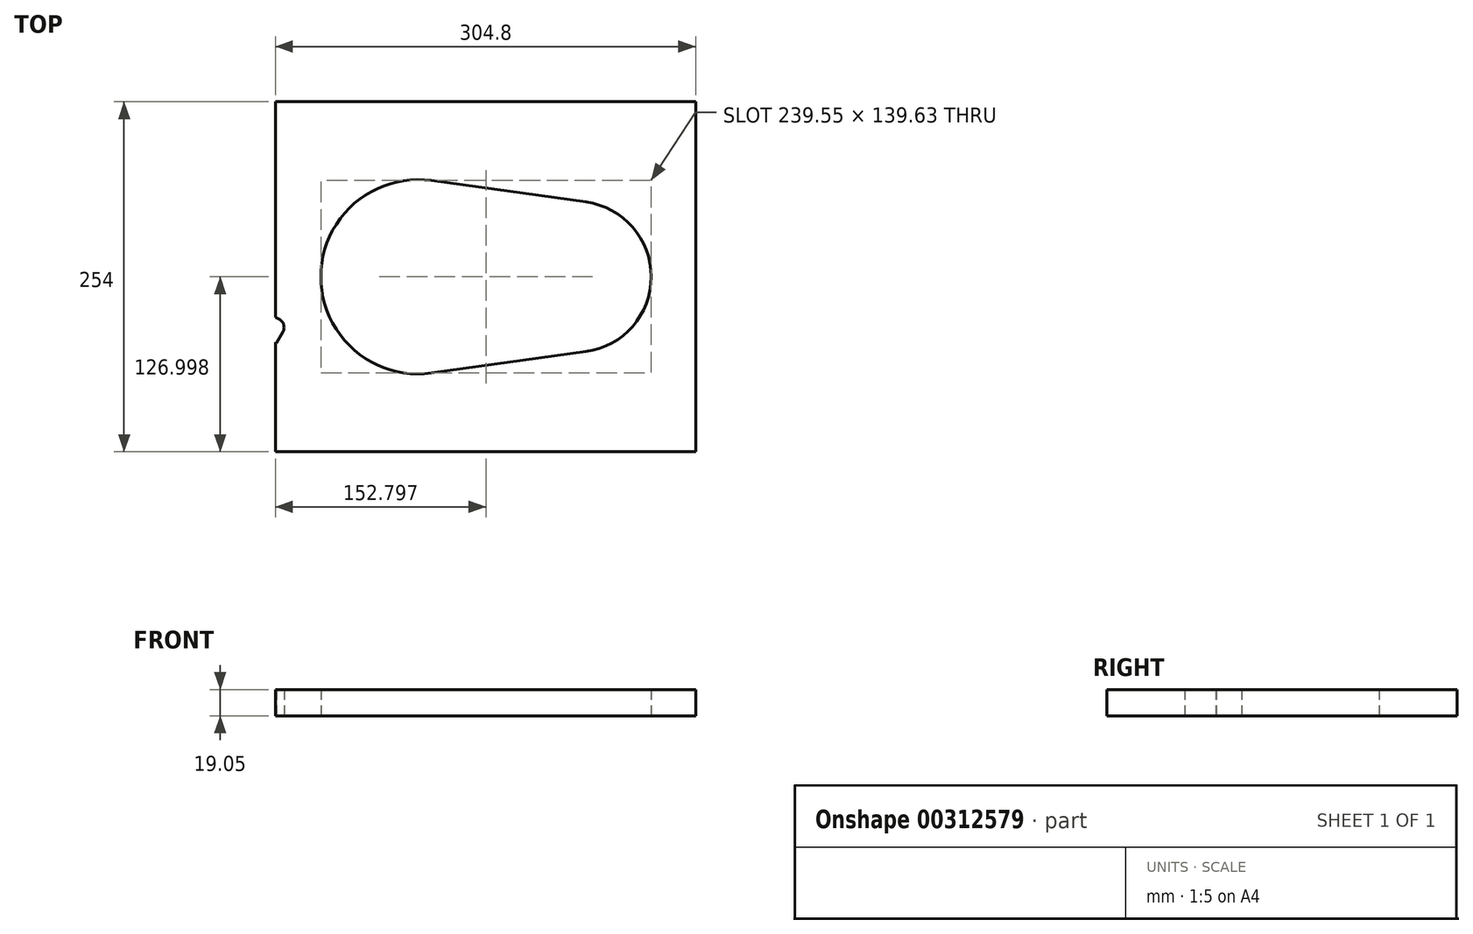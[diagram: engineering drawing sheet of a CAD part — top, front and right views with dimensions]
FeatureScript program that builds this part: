
annotation { "Feature Type Name" : "Feature", "Feature Type Description" : "" }
export const myFeature = defineFeature(function(context is Context, id is Id, definition is map)
    precondition{}
    {
        {
            var Q0;
            Q0=qCreatedBy(makeId("Top.planeOp"),FACE);
            var sketch = newSketch(context, id + "F0", { "sketchPlane" : qUnion([Q0])});
            skLineSegment(sketch, "E0", {"start": v(413.11, 329.58) * mm, "end": v(108.31, 329.58) * mm});
            skLineSegment(sketch, "E1", {"start": v(108.31, 329.58) * mm, "end": v(108.31, 75.58) * mm});
            skLineSegment(sketch, "E2", {"start": v(108.31, 75.58) * mm, "end": v(413.11, 75.58) * mm});
            skLineSegment(sketch, "E3", {"start": v(413.11, 329.58) * mm, "end": v(413.11, 75.58) * mm});
            skLineSegment(sketch, "E4", {"start": v(82.91, 329.58) * mm, "end": v(-221.89, 329.58) * mm});
            skLineSegment(sketch, "E5", {"start": v(-221.89, 329.58) * mm, "end": v(-221.89, 75.58) * mm});
            skLineSegment(sketch, "E6", {"start": v(-221.89, 75.58) * mm, "end": v(82.91, 75.58) * mm});
            skLineSegment(sketch, "E7", {"start": v(82.91, 329.58) * mm, "end": v(82.91, 75.58) * mm});
            skLineSegment(sketch, "E8", {"start": v(-173.23, 217.17) * mm, "end": v(-195.61, 223.17) * mm});
            skLineSegment(sketch, "E9", {"start": v(-173.23, 188) * mm, "end": v(-195.61, 182) * mm});
            skLineSegment(sketch, "E10", {"start": v(-195.61, 223.17) * mm, "end": v(-195.61, 182) * mm});
            skLineSegment(sketch, "E11", {"start": v(-133.37, 257.04) * mm, "end": v(-139.37, 279.42) * mm});
            skLineSegment(sketch, "E12", {"start": v(-104.19, 257.03) * mm, "end": v(-98.19, 279.42) * mm});
            skLineSegment(sketch, "E13", {"start": v(-98.19, 279.42) * mm, "end": v(-139.37, 279.42) * mm});
            skLineSegment(sketch, "E14", {"start": v(-133.37, 148.13) * mm, "end": v(-139.37, 125.75) * mm});
            skLineSegment(sketch, "E15", {"start": v(-104.19, 148.13) * mm, "end": v(-98.19, 125.75) * mm});
            skLineSegment(sketch, "E16", {"start": v(-98.19, 125.75) * mm, "end": v(-139.37, 125.75) * mm});
            skLineSegment(sketch, "E17", {"start": v(413.11, 68.19) * mm, "end": v(108.31, 68.19) * mm});
            skLineSegment(sketch, "E18", {"start": v(108.31, 68.19) * mm, "end": v(108.31, -185.81) * mm});
            skLineSegment(sketch, "E19", {"start": v(108.31, -185.81) * mm, "end": v(413.11, -185.81) * mm});
            skLineSegment(sketch, "E20", {"start": v(413.11, 68.19) * mm, "end": v(413.11, -185.81) * mm});
            skLineSegment(sketch, "E21", {"start": v(82.91, 68.19) * mm, "end": v(82.91, -185.81) * mm});
            skLineSegment(sketch, "E22", {"start": v(-221.89, -185.81) * mm, "end": v(82.91, -185.81) * mm});
            skLineSegment(sketch, "E23", {"start": v(-221.89, 68.19) * mm, "end": v(-221.89, -185.81) * mm});
            skLineSegment(sketch, "E24", {"start": v(82.91, 68.19) * mm, "end": v(-221.89, 68.19) * mm});
            skLineSegment(sketch, "E25", {"start": v(324.6, -113.27) * mm, "end": v(330.6, -135.65) * mm});
            skLineSegment(sketch, "E26", {"start": v(295.42, -113.26) * mm, "end": v(289.42, -135.65) * mm});
            skLineSegment(sketch, "E27", {"start": v(289.42, -135.65) * mm, "end": v(330.6, -135.65) * mm});
            skLineSegment(sketch, "E28", {"start": v(82.91, -136.8) * mm, "end": v(108.31, -136.8) * mm});
            skArc(sketch, "E29", {"start": v(187.78, 272.39) * mm, "mid": v(140.54, 218.14) * mm, "end": v(187.78, 163.9) * mm});
            skLineSegment(sketch, "E30", {"start": v(187.78, 163.9) * mm, "end": v(274.13, 151.9) * mm});
            skArc(sketch, "E31", {"start": v(274.13, 151.9) * mm, "mid": v(285.88, 145.55) * mm, "end": v(290.56, 133.04) * mm});
            skLineSegment(sketch, "E32", {"start": v(290.56, 133.04) * mm, "end": v(290.56, 122.9) * mm});
            skArc(sketch, "E33", {"start": v(290.56, 122.9) * mm, "mid": v(292.42, 118.4) * mm, "end": v(296.91, 116.54) * mm});
            skLineSegment(sketch, "E34", {"start": v(296.91, 116.54) * mm, "end": v(306.44, 116.54) * mm});
            skLineSegment(sketch, "E35", {"start": v(306.44, 116.54) * mm, "end": v(306.44, 173.17) * mm});
            skArc(sketch, "E36", {"start": v(306.44, 173.17) * mm, "mid": v(309.61, 263.23) * mm, "end": v(312.79, 173.17) * mm});
            skLineSegment(sketch, "E37", {"start": v(312.79, 173.17) * mm, "end": v(312.79, 116.54) * mm});
            skLineSegment(sketch, "E38", {"start": v(312.79, 116.54) * mm, "end": v(322.31, 116.54) * mm});
            skArc(sketch, "E39", {"start": v(322.31, 116.54) * mm, "mid": v(326.8, 118.4) * mm, "end": v(328.66, 122.9) * mm});
            skLineSegment(sketch, "E40", {"start": v(328.66, 122.9) * mm, "end": v(328.66, 137.12) * mm});
            skArc(sketch, "E41", {"start": v(328.66, 137.12) * mm, "mid": v(331.63, 147.33) * mm, "end": v(339.6, 154.36) * mm});
            skArc(sketch, "E42", {"start": v(339.6, 154.36) * mm, "mid": v(377.18, 238.21) * mm, "end": v(299.92, 287.96) * mm});
            skLineSegment(sketch, "E43", {"start": v(299.92, 287.96) * mm, "end": v(187.78, 272.39) * mm});
            skLineSegment(sketch, "E44", {"start": v(3.05, 256.83) * mm, "end": v(-109.09, 272.4) * mm});
            skArc(sketch, "E45", {"start": v(-109.09, 272.4) * mm, "mid": v(-189.26, 202.58) * mm, "end": v(-109.1, 132.77) * mm});
            skLineSegment(sketch, "E46", {"start": v(-109.1, 132.77) * mm, "end": v(3.05, 148.33) * mm});
            skArc(sketch, "E47", {"start": v(3.05, 148.33) * mm, "mid": v(50.3, 202.58) * mm, "end": v(3.05, 256.83) * mm});
            skArc(sketch, "E48", {"start": v(-25.36, 170.03) * mm, "mid": v(2.98, 202.58) * mm, "end": v(-25.36, 235.13) * mm});
            skLineSegment(sketch, "E49", {"start": v(-25.36, 235.13) * mm, "end": v(-68.73, 241.15) * mm});
            skArc(sketch, "E50", {"start": v(-68.73, 241.15) * mm, "mid": v(-71.88, 239.65) * mm, "end": v(-71.75, 236.16) * mm});
            skArc(sketch, "E51", {"start": v(-71.75, 236.16) * mm, "mid": v(-61, 202.58) * mm, "end": v(-71.75, 169) * mm});
            skArc(sketch, "E52", {"start": v(-71.75, 169) * mm, "mid": v(-71.88, 165.51) * mm, "end": v(-68.73, 164.01) * mm});
            skLineSegment(sketch, "E53", {"start": v(-68.73, 164.01) * mm, "end": v(-25.36, 170.03) * mm});
            skLineSegment(sketch, "E54", {"start": v(188.18, -4.56) * mm, "end": v(300.31, 11) * mm});
            skArc(sketch, "E55", {"start": v(300.31, 11) * mm, "mid": v(380.5, -58.81) * mm, "end": v(300.32, -128.63) * mm});
            skLineSegment(sketch, "E56", {"start": v(300.32, -128.63) * mm, "end": v(188.18, -113.06) * mm});
            skArc(sketch, "E57", {"start": v(188.18, -113.06) * mm, "mid": v(140.94, -58.81) * mm, "end": v(188.18, -4.56) * mm});
            skArc(sketch, "E58", {"start": v(216.59, -91.36) * mm, "mid": v(188.24, -58.81) * mm, "end": v(216.59, -26.26) * mm});
            skLineSegment(sketch, "E59", {"start": v(216.59, -26.26) * mm, "end": v(259.96, -20.24) * mm});
            skArc(sketch, "E60", {"start": v(259.96, -20.24) * mm, "mid": v(263.11, -21.74) * mm, "end": v(262.98, -25.23) * mm});
            skArc(sketch, "E61", {"start": v(262.98, -25.23) * mm, "mid": v(252.22, -58.81) * mm, "end": v(262.98, -92.4) * mm});
            skArc(sketch, "E62", {"start": v(262.98, -92.4) * mm, "mid": v(263.11, -95.88) * mm, "end": v(259.96, -97.38) * mm});
            skLineSegment(sketch, "E63", {"start": v(259.96, -97.38) * mm, "end": v(216.59, -91.36) * mm});
            skArc(sketch, "E64", {"start": v(-270.48, -116.68) * mm, "mid": v(-307.76, -129.24) * mm, "end": v(-345.97, -119.85) * mm});
            skArc(sketch, "E65", {"start": v(-345.97, -119.85) * mm, "mid": v(-364.21, -104.72) * mm, "end": v(-376.4, -84.39) * mm});
            skArc(sketch, "E66", {"start": v(-376.4, -84.39) * mm, "mid": v(-379.7, -78.9) * mm, "end": v(-384.63, -74.8) * mm});
            skLineSegment(sketch, "E67", {"start": v(-384.63, -74.8) * mm, "end": v(-413.11, -58.36) * mm});
            skLineSegment(sketch, "E68", {"start": v(-413.11, -58.36) * mm, "end": v(-362.31, 29.63) * mm});
            skLineSegment(sketch, "E69", {"start": v(-362.31, 29.63) * mm, "end": v(-333.83, 13.19) * mm});
            skArc(sketch, "E70", {"start": v(-333.83, 13.19) * mm, "mid": v(-327.82, 10.96) * mm, "end": v(-321.42, 10.86) * mm});
            skArc(sketch, "E71", {"start": v(-321.42, 10.86) * mm, "mid": v(-297.71, 10.46) * mm, "end": v(-275.48, 2.23) * mm});
            skArc(sketch, "E72", {"start": v(-275.48, 2.23) * mm, "mid": v(-248.26, -26.17) * mm, "end": v(-240.49, -64.73) * mm});
            skArc(sketch, "E73", {"start": v(-240.49, -64.73) * mm, "mid": v(-238.39, -75.15) * mm, "end": v(-231.03, -82.83) * mm});
            skLineSegment(sketch, "E74", {"start": v(-231.03, -82.83) * mm, "end": v(-218.71, -89.94) * mm});
            skArc(sketch, "E75", {"start": v(-218.71, -89.94) * mm, "mid": v(-215.75, -93.8) * mm, "end": v(-216.39, -98.61) * mm});
            skLineSegment(sketch, "E76", {"start": v(-216.39, -98.61) * mm, "end": v(-221.15, -106.86) * mm});
            skLineSegment(sketch, "E77", {"start": v(-221.15, -106.86) * mm, "end": v(-270.19, -78.55) * mm});
            skArc(sketch, "E78", {"start": v(-270.19, -78.55) * mm, "mid": v(-266.47, -67.42) * mm, "end": v(-265.75, -55.7) * mm});
            skArc(sketch, "E79", {"start": v(-265.75, -55.7) * mm, "mid": v(-265.37, -53.97) * mm, "end": v(-264.11, -52.7) * mm});
            skArc(sketch, "E80", {"start": v(-264.11, -52.7) * mm, "mid": v(-261.04, -45.5) * mm, "end": v(-267.3, -40.8) * mm});
            skArc(sketch, "E81", {"start": v(-267.3, -40.8) * mm, "mid": v(-269.02, -40.33) * mm, "end": v(-270.22, -39.01) * mm});
            skArc(sketch, "E82", {"start": v(-270.22, -39.01) * mm, "mid": v(-288.18, -19.77) * mm, "end": v(-313.83, -13.83) * mm});
            skArc(sketch, "E83", {"start": v(-313.83, -13.83) * mm, "mid": v(-315.57, -13.45) * mm, "end": v(-316.83, -12.2) * mm});
            skArc(sketch, "E84", {"start": v(-316.83, -12.2) * mm, "mid": v(-324.04, -9.13) * mm, "end": v(-328.74, -15.4) * mm});
            skArc(sketch, "E85", {"start": v(-328.74, -15.4) * mm, "mid": v(-329.2, -17.1) * mm, "end": v(-330.52, -18.3) * mm});
            skArc(sketch, "E86", {"start": v(-330.52, -18.3) * mm, "mid": v(-349.77, -36.27) * mm, "end": v(-355.7, -61.92) * mm});
            skArc(sketch, "E87", {"start": v(-355.7, -61.92) * mm, "mid": v(-356.08, -63.66) * mm, "end": v(-357.34, -64.92) * mm});
            skArc(sketch, "E88", {"start": v(-357.34, -64.92) * mm, "mid": v(-360.4, -72.12) * mm, "end": v(-354.15, -76.83) * mm});
            skArc(sketch, "E89", {"start": v(-354.15, -76.83) * mm, "mid": v(-352.43, -77.3) * mm, "end": v(-351.23, -78.61) * mm});
            skArc(sketch, "E90", {"start": v(-351.23, -78.61) * mm, "mid": v(-333.27, -97.86) * mm, "end": v(-307.62, -103.8) * mm});
            skArc(sketch, "E91", {"start": v(-307.62, -103.8) * mm, "mid": v(-305.88, -104.17) * mm, "end": v(-304.62, -105.43) * mm});
            skArc(sketch, "E92", {"start": v(-304.62, -105.43) * mm, "mid": v(-297.41, -108.5) * mm, "end": v(-292.7, -102.23) * mm});
            skArc(sketch, "E93", {"start": v(-292.7, -102.23) * mm, "mid": v(-292.24, -100.52) * mm, "end": v(-290.93, -99.32) * mm});
            skArc(sketch, "E94", {"start": v(-290.93, -99.32) * mm, "mid": v(-281.14, -92.84) * mm, "end": v(-273.36, -84.05) * mm});
            skLineSegment(sketch, "E95", {"start": v(-273.36, -84.05) * mm, "end": v(-224.32, -112.36) * mm});
            skLineSegment(sketch, "E96", {"start": v(-224.32, -112.36) * mm, "end": v(-229.09, -120.61) * mm});
            skArc(sketch, "E97", {"start": v(-229.09, -120.61) * mm, "mid": v(-232.94, -123.57) * mm, "end": v(-237.76, -122.94) * mm});
            skLineSegment(sketch, "E98", {"start": v(-237.76, -122.94) * mm, "end": v(-250.08, -115.82) * mm});
            skArc(sketch, "E99", {"start": v(-250.08, -115.82) * mm, "mid": v(-260.4, -113.29) * mm, "end": v(-270.48, -116.68) * mm});
            skLineSegment(sketch, "E100", {"start": v(-108.7, 11) * mm, "end": v(3.45, -4.56) * mm});
            skArc(sketch, "E101", {"start": v(3.45, -4.56) * mm, "mid": v(50.68, -58.81) * mm, "end": v(3.45, -113.06) * mm});
            skLineSegment(sketch, "E102", {"start": v(3.45, -113.06) * mm, "end": v(-108.7, -128.63) * mm});
            skArc(sketch, "E103", {"start": v(-108.7, -128.63) * mm, "mid": v(-188.87, -58.81) * mm, "end": v(-108.7, 11) * mm});
            skLineSegment(sketch, "E104", {"start": v(-108.7, -189.28) * mm, "end": v(3.45, -204.85) * mm});
            skArc(sketch, "E105", {"start": v(3.45, -204.85) * mm, "mid": v(50.68, -259.1) * mm, "end": v(3.45, -313.35) * mm});
            skLineSegment(sketch, "E106", {"start": v(3.45, -313.35) * mm, "end": v(-108.7, -328.91) * mm});
            skArc(sketch, "E107", {"start": v(-108.7, -328.91) * mm, "mid": v(-188.87, -259.1) * mm, "end": v(-108.7, -189.28) * mm});
            skCircle(sketch, "E108", {"center": v(153.24, 218.14) * mm, "radius": 4.76 * mm});
            skCircle(sketch, "E109", {"center": v(195.31, 218.14) * mm, "radius": 29.37 * mm});
            skCircle(sketch, "E110", {"center": v(350.47, 177.28) * mm, "radius": 4.76 * mm});
            skCircle(sketch, "E111", {"center": v(350.47, 259) * mm, "radius": 4.76 * mm});
            skCircle(sketch, "E112", {"center": v(245.6, 267.6) * mm, "radius": 4.76 * mm});
            skCircle(sketch, "E113", {"center": v(245.6, 168.69) * mm, "radius": 4.76 * mm});
            skCircle(sketch, "E114", {"center": v(37.6, 202.58) * mm, "radius": 4.76 * mm});
            skCircle(sketch, "E115", {"center": v(-159.64, 161.72) * mm, "radius": 4.76 * mm});
            skCircle(sketch, "E116", {"center": v(-159.64, 243.44) * mm, "radius": 4.76 * mm});
            skCircle(sketch, "E117", {"center": v(-54.76, 252.04) * mm, "radius": 4.76 * mm});
            skCircle(sketch, "E118", {"center": v(-54.76, 153.13) * mm, "radius": 4.76 * mm});
            skCircle(sketch, "E119", {"center": v(-118.78, 202.58) * mm, "radius": 19.05 * mm});
            skArc(sketch, "E120", {"start": v(-158.7, 181.63) * mm, "mid": v(-150.66, 170.7) * mm, "end": v(-139.73, 162.66) * mm});
            skArc(sketch, "E121", {"start": v(-173.23, 217.17) * mm, "mid": v(-164.85, 217.8) * mm, "end": v(-158.7, 223.54) * mm});
            skArc(sketch, "E122", {"start": v(-139.73, 242.5) * mm, "mid": v(-134, 248.65) * mm, "end": v(-133.37, 257.03) * mm});
            skArc(sketch, "E123", {"start": v(-104.19, 257.03) * mm, "mid": v(-103.55, 248.65) * mm, "end": v(-97.82, 242.5) * mm});
            skArc(sketch, "E124", {"start": v(-133.37, 148.13) * mm, "mid": v(-134, 156.51) * mm, "end": v(-139.73, 162.66) * mm});
            skArc(sketch, "E125", {"start": v(-97.82, 162.66) * mm, "mid": v(-103.55, 156.51) * mm, "end": v(-104.19, 148.13) * mm});
            skArc(sketch, "E126", {"start": v(-158.7, 181.63) * mm, "mid": v(-164.85, 187.36) * mm, "end": v(-173.23, 188) * mm});
            skArc(sketch, "E127", {"start": v(-139.73, 242.5) * mm, "mid": v(-150.66, 234.46) * mm, "end": v(-158.7, 223.54) * mm});
            skArc(sketch, "E128", {"start": v(-97.82, 162.66) * mm, "mid": v(-73.7, 202.58) * mm, "end": v(-97.82, 242.5) * mm});
            skCircle(sketch, "E129", {"center": v(-4.08, -58.81) * mm, "radius": 29.37 * mm});
            skCircle(sketch, "E130", {"center": v(310, -58.81) * mm, "radius": 19.05 * mm});
            skArc(sketch, "E131", {"start": v(330.96, -98.73) * mm, "mid": v(325.23, -104.88) * mm, "end": v(324.6, -113.26) * mm});
            skArc(sketch, "E132", {"start": v(295.42, -113.26) * mm, "mid": v(294.78, -104.88) * mm, "end": v(289.05, -98.73) * mm});
            skArc(sketch, "E133", {"start": v(330.96, -98.73) * mm, "mid": v(310, -13.73) * mm, "end": v(289.05, -98.73) * mm});
            skCircle(sketch, "E134", {"center": v(25.66, -29.07) * mm, "radius": 9.53 * mm});
            skCircle(sketch, "E135", {"center": v(-54.37, -9.36) * mm, "radius": 9.53 * mm});
            skCircle(sketch, "E136", {"center": v(-54.37, -108.27) * mm, "radius": 9.53 * mm});
            skCircle(sketch, "E137", {"center": v(-159.24, -17.95) * mm, "radius": 9.53 * mm});
            skCircle(sketch, "E138", {"center": v(-89.5, -8.77) * mm, "radius": 4.76 * mm});
            skCircle(sketch, "E139", {"center": v(-147.28, -108.86) * mm, "radius": 4.76 * mm});
            skCircle(sketch, "E140", {"center": v(-118.38, -58.81) * mm, "radius": 46.04 * mm});
            skCircle(sketch, "E141", {"center": v(25.66, -88.56) * mm, "radius": 9.53 * mm});
            skCircle(sketch, "E142", {"center": v(-159.24, -99.67) * mm, "radius": 9.53 * mm});
            skCircle(sketch, "E143", {"center": v(-4.08, -259.1) * mm, "radius": 29.37 * mm});
            skCircle(sketch, "E144", {"center": v(25.66, -229.35) * mm, "radius": 9.53 * mm});
            skCircle(sketch, "E145", {"center": v(-54.37, -209.65) * mm, "radius": 9.53 * mm});
            skCircle(sketch, "E146", {"center": v(-54.37, -308.55) * mm, "radius": 9.53 * mm});
            skCircle(sketch, "E147", {"center": v(-159.24, -218.24) * mm, "radius": 9.53 * mm});
            skCircle(sketch, "E148", {"center": v(-89.5, -209.05) * mm, "radius": 4.76 * mm});
            skCircle(sketch, "E149", {"center": v(-147.28, -309.14) * mm, "radius": 4.76 * mm});
            skCircle(sketch, "E150", {"center": v(-118.38, -259.1) * mm, "radius": 46.04 * mm});
            skCircle(sketch, "E151", {"center": v(25.66, -288.84) * mm, "radius": 9.53 * mm});
            skCircle(sketch, "E152", {"center": v(-159.24, -299.96) * mm, "radius": 9.53 * mm});
            skCircle(sketch, "E153", {"center": v(350.47, -17.95) * mm, "radius": 9.53 * mm});
            skCircle(sketch, "E154", {"center": v(245.6, -9.36) * mm, "radius": 9.53 * mm});
            skCircle(sketch, "E155", {"center": v(165.57, -29.07) * mm, "radius": 9.53 * mm});
            skCircle(sketch, "E156", {"center": v(165.57, -88.56) * mm, "radius": 9.53 * mm});
            skCircle(sketch, "E157", {"center": v(245.6, -108.27) * mm, "radius": 9.53 * mm});
            skCircle(sketch, "E158", {"center": v(350.47, -99.67) * mm, "radius": 9.53 * mm});
            skCircle(sketch, "E159", {"center": v(-281.83, -8.77) * mm, "radius": 4.76 * mm});
            skCircle(sketch, "E160", {"center": v(-339.62, -108.86) * mm, "radius": 4.76 * mm});
            skSolve(sketch);
        }
        {
            var Q0;
            Q0=makeQuery(id+"F0.imprint","IMPRINT",FACE,{"disambiguationData":[TD([[makeQuery(id+"F0.imprint","IMPRINT",EDGE,{"derivedFrom":sQuery(id+"F0.wireOp",EDGE,"E64")}),-1.0]])]});
            var Q1;
            {var subQ1=sQuery(id+"F0.wireOp",EDGE,"E75");Q1=makeQuery(id+"F0.imprint","IMPRINT",FACE,{"disambiguationData":[TD([[makeQuery(id+"F0.imprint","IMPRINT",EDGE,{"derivedFrom":subQ1}),-1.0]])]});}
            extrude(context, id + "F1", {"entities" : qUnion([Q0, Q1]), "depth" : 19.05 * mm});
        }
    });
